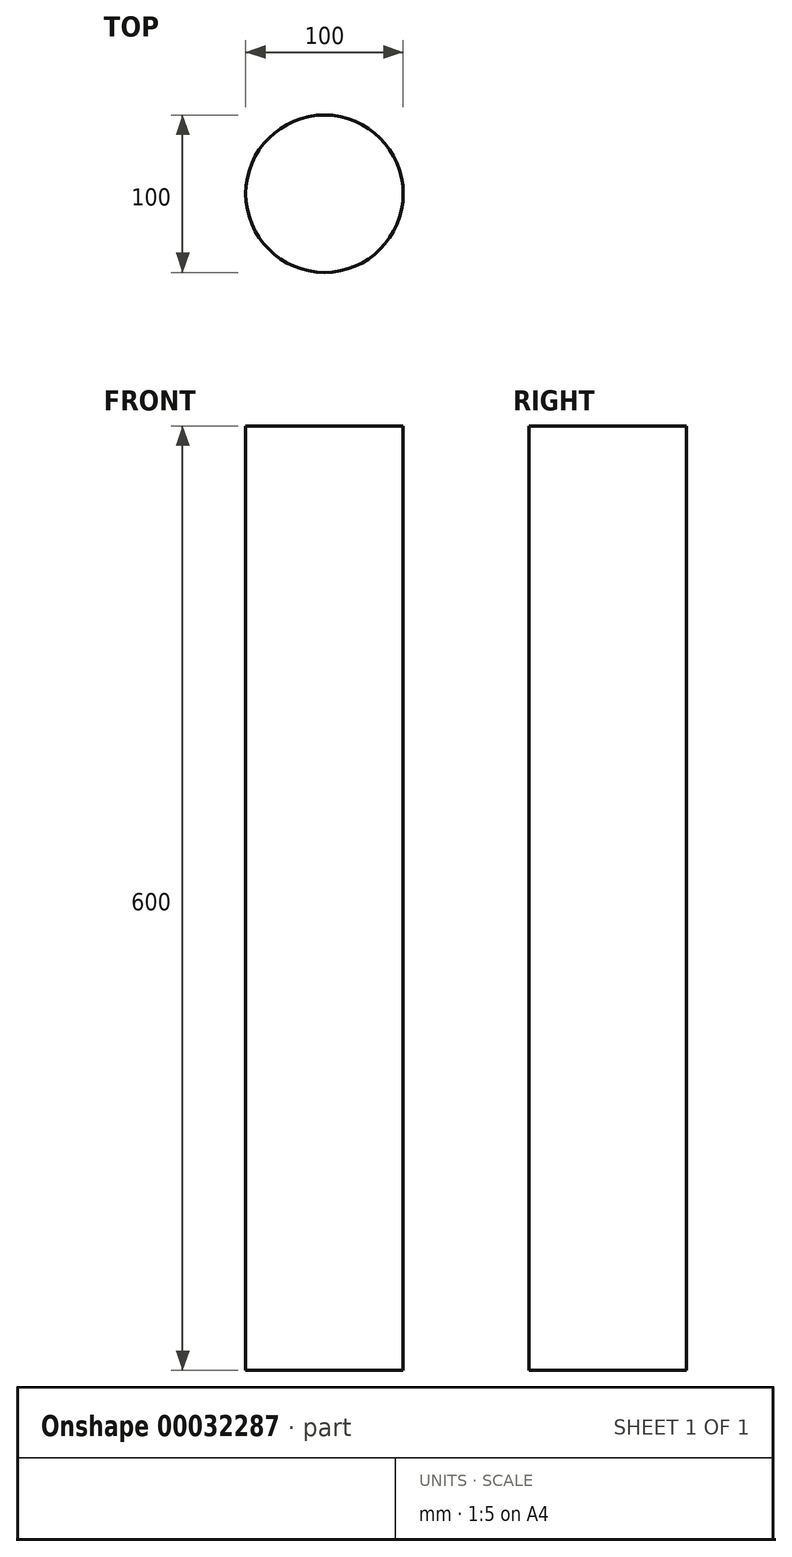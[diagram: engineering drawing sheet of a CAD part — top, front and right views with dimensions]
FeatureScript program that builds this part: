
annotation { "Feature Type Name" : "Feature", "Feature Type Description" : "" }
export const myFeature = defineFeature(function(context is Context, id is Id, definition is map)
    precondition{}
    {
        {
            var Q0;
            Q0=qCreatedBy(makeId("Top.planeOp"),FACE);
            var sketch = newSketch(context, id + "F0", { "sketchPlane" : qUnion([Q0])});
            skCircle(sketch, "E0", {"center": v(0, 0) * mm, "radius": 50 * mm});
            skSolve(sketch);
        }
        {
            var Q0;
            Q0=sQuery(id+"F0.wireOp",EDGE,"E0");
            extrude(context, id + "F1", {"bodyType" : ToolBodyType.SURFACE, "surfaceEntities" : qUnion([Q0]), "depth" : 600 * mm});
        }
    });
